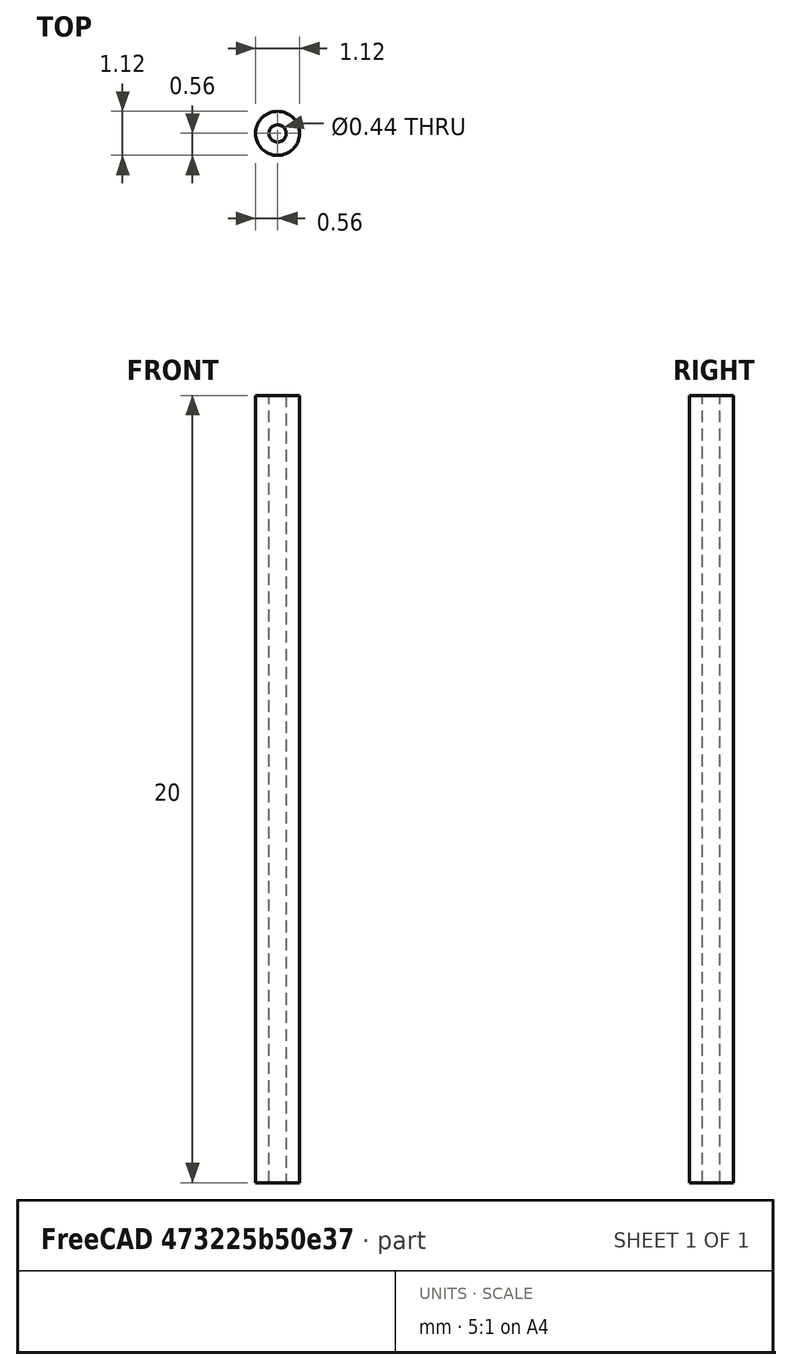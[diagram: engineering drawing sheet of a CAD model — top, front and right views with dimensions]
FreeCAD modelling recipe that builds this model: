
FCSTD DOCUMENT  (FreeCAD 0.20R29603 (Git))
Label: CableCase
License: All rights reserved
LicenseURL: http://en.wikipedia.org/wiki/All_rights_reserved
objects: PartDesign::AdditiveCylinder×1, Sketcher::SketchObject×1, PartDesign::Pocket×1, PartDesign::Body×1
note: 6 computed .brp shape members not serialized (recipe doc carries the construction recipe); baked Part::Feature solids carry a one-line shape summary decoded from their .brp

FEATURE [PartDesign::AdditiveCylinder] Cylinder
  Angle = 360
  AttacherType = Attacher::AttachEngine3D
  FirstAngle = 0
  Height = 20
  MapMode = 5
  Radius = 0.56
  Refine = true
  SecondAngle = 0
  Support = -> [XY_Plane]
FEATURE [Sketcher::SketchObject] Sketch
  FullyConstrained = true
  MapMode = 5
  Placement = pos=(0,0,20) rot=(0,0,1;0rad)
  Support = -> [Cylinder]
  sketch-geometry (1):
    g0: Circle CenterX=0 CenterY=0 CenterZ=0 NormalX=0 NormalY=0 NormalZ=1 AngleXU=0 Radius=0.218838
  constraints (2):
    c: Coincident(g0,g-1)
    c: Diameter(g0) = 0.437676
FEATURE [PartDesign::Pocket] Pocket
  BaseFeature = -> Cylinder
  Direction = (0,0,-1)
  Length = 5
  Length2 = 5
  Profile = -> Sketch
  ReferenceAxis = -> Sketch [N_Axis]
  Refine = true
  Type = 1
FEATURE [PartDesign::Body] Body
  Group = -> [Cylinder,Sketch,Pocket]
  Origin = -> Origin
  Tip = -> Pocket
